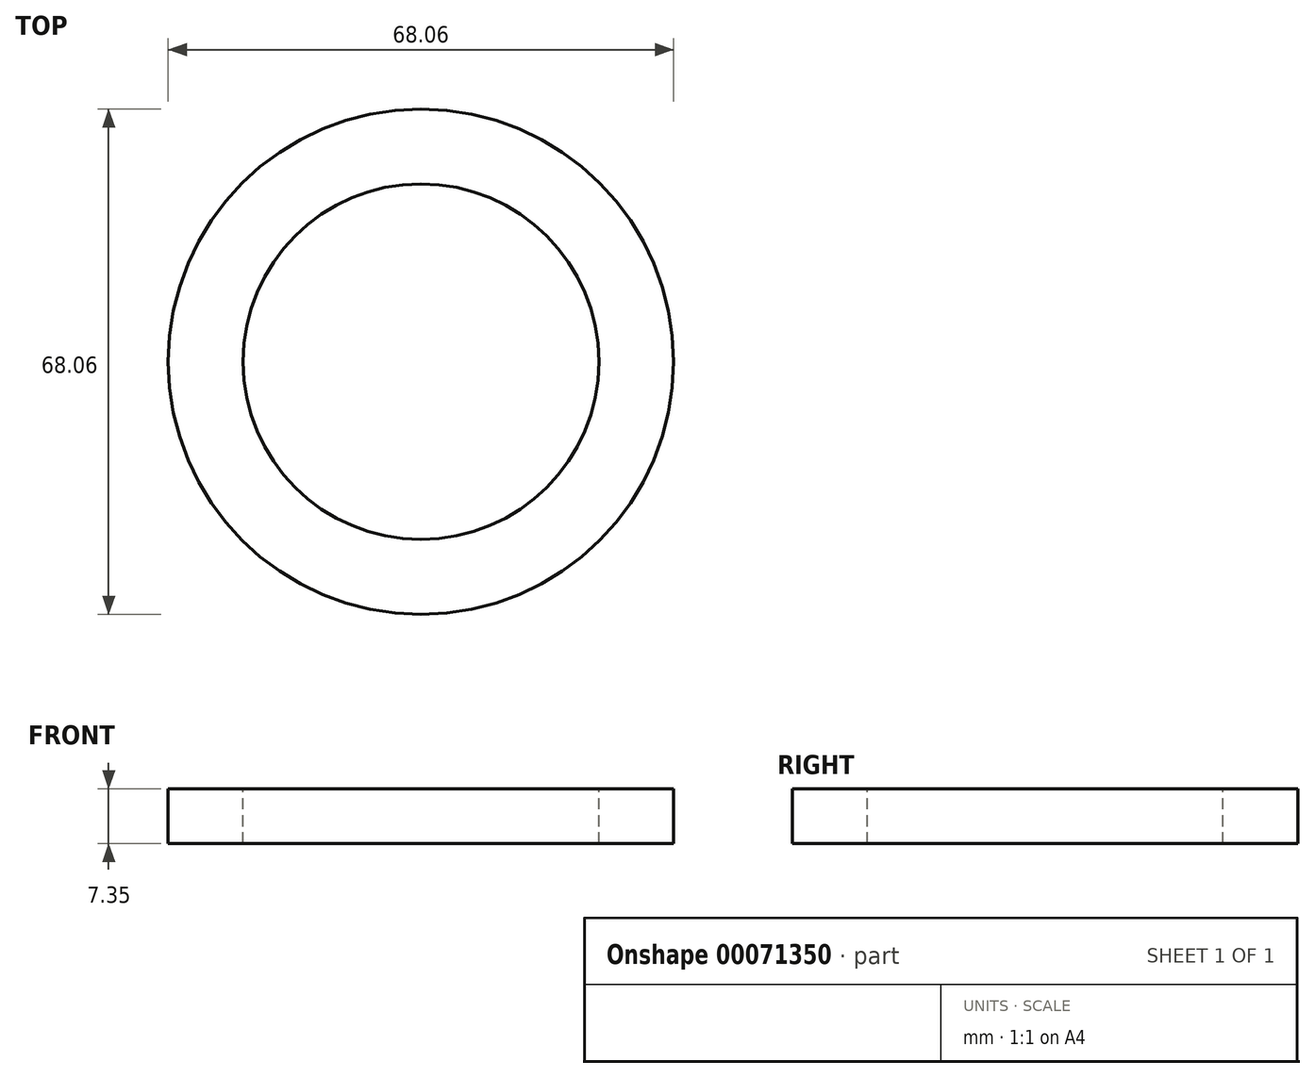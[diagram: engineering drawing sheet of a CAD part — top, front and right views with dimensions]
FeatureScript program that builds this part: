
annotation { "Feature Type Name" : "Feature", "Feature Type Description" : "" }
export const myFeature = defineFeature(function(context is Context, id is Id, definition is map)
    precondition{}
    {
        {
            var Q0;
            Q0=qCreatedBy(makeId("Top.planeOp"),FACE);
            var sketch = newSketch(context, id + "F0", { "sketchPlane" : qUnion([Q0])});
            skCircle(sketch, "E0", {"center": v(0, 0) * mm, "radius": 23.95 * mm});
            skCircle(sketch, "E1", {"center": v(0, 0) * mm, "radius": 34.03 * mm});
            skCircle(sketch, "E2", {"center": v(0, 0) * mm, "radius": 4.94 * mm});
            skCircle(sketch, "E3", {"center": v(-2.24, 2.31) * mm, "radius": 1.4 * mm});
            skSolve(sketch);
        }
        {
            var Q0;
            Q0=sQuery(id+"F0.wireOp",EDGE,"E1");
            var Q1;
            Q1=sQuery(id+"F0.wireOp",EDGE,"E0");
            extrude(context, id + "F1", {"bodyType" : ToolBodyType.SURFACE, "surfaceEntities" : qUnion([Q0, Q1]), "depth" : 7.35 * mm});
        }
    });
